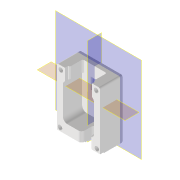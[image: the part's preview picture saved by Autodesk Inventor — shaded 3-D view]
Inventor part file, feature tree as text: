
AUTODESK INVENTOR PART (.ipt)
format: ipt  version: 2022 (Build 260153000, 153)  size: 440,320 bytes
history: native  units: mm
features: reference x19, other x12, sketch x10, extrude x9, plane x5, projected_geometry x5, fillet x2, hole x2, chamfer x1
ambient origin geometry x8: Origin, YZ Plane, XZ Plane, XY Plane, X Axis, Y Axis, Z Axis, Center Point
bodies: Solid1 (feature_tree)
feature tree (65):
  plane  "Work Plane1"
  extrude  "Extrusion1"  Depth=53.8mm
  extrude  "IM_offset"  Depth=53.8mm
  plane  "Arbeitsebene5"
  plane  "Arbeitsebene6"
  extrude  "Extrusion26"  Depth=45.0mm
  chamfer  "Fase2"  Distance=0.1mm
  plane  "Arbeitsebene9"
  extrude  "Extrusion29"  Depth=0.5mm
  extrude  "Extrusion30"  Depth=0.5mm
  plane  "Arbeitsebene10"
  extrude  "Extrusion31"  Depth=0.5mm
  fillet  "Rundung3"  Radius=10.0mm
  hole  "Bohrung2"  [1 undecoded]
  extrude  "Extrusion32"  Depth=10.0mm TaperAngle=0.0deg
  hole  "Bohrung3"  [1 undecoded]
  extrude  "Extrusion33"  [1 undecoded]
  extrude  "Extrusion34"  Depth=0.5mm
  fillet  "Rundung4"  Radius=8.6mm
  sketch  "Sketch1"  dims[d10=12.0mm d11=0.0mm d18=53.8mm]
  reference  "Reference1"
  reference  "Reference2"
  reference  "Reference3"
  reference  "Reference4"
  reference  "Reference9"
  reference  "Reference20"
  reference  "Reference21"
  reference  "Reference22"
  reference  "Reference23"
  reference  "Reference24"
  sketch  "Skizze4"  dims[d19=45.0deg d20=53.8mm]
  projected_geometry  "Projizierte Kontur1"
  sketch  "Skizze31"  dims[d21=45.0mm d22=45.0mm]
  projected_geometry  "Projizierte Kontur17"
  sketch  "Skizze34"  dims[d30=20.0mm]
  reference  "Referenz35"
  sketch  "Skizze35"  dims[d31=20.0mm]
  reference  "Referenz36"
  reference  "Referenz37"
  reference  "Referenz38"
  reference  "Referenz39"
  reference  "Referenz40"
  sketch  "Skizze37"  dims[d32=2.8mm]
  projected_geometry  "Projizierte Kontur18"
  reference  "Referenz41"
  sketch  "Skizze38"  dims[d33=2.8mm]
  reference  "Referenz42"
  sketch  "Skizze39"  dims[d34=2.8mm]
  reference  "Referenz43"
  sketch  "Skizze40"  dims[d35=3.0mm]
  projected_geometry  "Projizierte Kontur19"
  sketch  "Skizze41"  dims[d36=0.1mm d37=0.1mm d38=0.1mm d39=0.1mm d40=0.2mm d41=10.0mm d42=0.0mm d181=7.5mm d182=10.0mm d183=0.0mm d184=0.5mm d185=2.0mm d186=45.0deg d193=-1.5mm d194=8.6mm d195=8.6mm d196=0.0mm d197=0.0mm d198=10.0mm d199=0.0mm d200=4.0mm d201=12.0mm d202=0.0mm d203=1.0mm d204=30.0mm d205=30.0mm d206=2.8mm d207=6.0mm d208=8.0mm d209=6.0mm d210=90.0deg d211=8.0mm d212=20.594885mm d213=0.0mm d214=0.0mm d215=2.8mm d216=6.0mm d217=4.0mm d218=2.0mm d219=90.0deg d220=8.0mm d221=20.594885mm d222=2.0mm d223=0.0mm d224=1.0mm d225=5.0mm d226=8.0mm d227=10.0mm d228=0.0mm d229=2.0mm d160=0.5mm d161=0.872665mm d162=0.5mm d163=0.872665mm]
  projected_geometry  "Projizierte Kontur20"
  other  "Assembly_Cube_v2_Thorlabs.iam"
  other  "10_Cube_Base:1"
  other  "00_Base_v0:1"
  other  "Assembly_Cube_Kinematic_Mirrormount_v2.iam"
  other  "Assembly_Cube_empty_1x1_v2:1"
  other  "10_Cube_1x1_v2:1"
  other  "10_Lid_1x1_v2:1"
  other  "Assembly_Cube_SEEED_Xiao_Sense_Camera_v3.iam"
  other  "00_Seeeduino Xiao:1"
  other  "00_ESP3-CAM:1"
  other  "00_ESP32_XIAO_Adapter_lid:1"
  other  "10_Cube_Lid:1"
note: 3 required parameter values undecoded (feature->parameter linkage not recoverable at this tier; creation-order binding heuristic only, values carry confidence <= 0.55)
